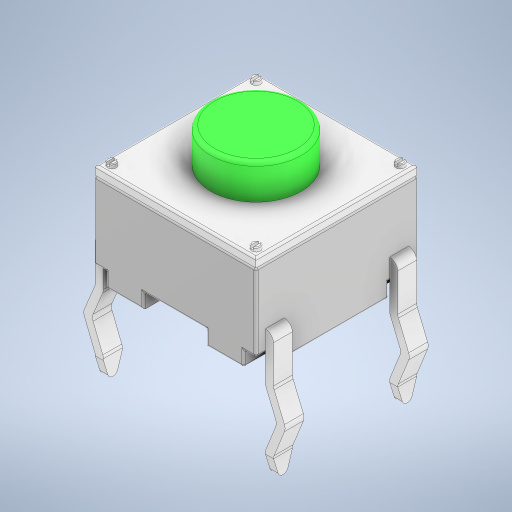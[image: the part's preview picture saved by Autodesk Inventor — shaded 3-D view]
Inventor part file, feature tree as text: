
AUTODESK INVENTOR PART (.ipt)
format: ipt  version: 2024.3 (Build 283343000, 343)  size: 496,128 bytes
history: native  units: in
note: dims shown in document units (in); Inventor stores cm internally (conversion verified against a paired STEP export)
features: other x4, fillet x3
ambient origin geometry x8: Origin, YZ Plane, XZ Plane, XY Plane, X Axis, Y Axis, Z Axis, Center Point
bodies: Solid1 (feature_tree), Solid2 (feature_tree), Solid3 (feature_tree), Solid4 (feature_tree), Solid5 (feature_tree), Solid6 (feature_tree), Solid7 (feature_tree)
feature tree (7):
  fillet  "Fillet5"  [1 undecoded]
  fillet  "Fillet7"  [1 undecoded]
  fillet  "Fillet8"  [1 undecoded]
  other  "Cut-Extrude7[1]"
  other  "Cut-Extrude7[2]"
  other  "Cut-Extrude7[3]"
  other  "Cut-Extrude7[4]"
note: 3 required parameter values undecoded (feature->parameter linkage not recoverable at this tier; creation-order binding heuristic only, values carry confidence <= 0.55)
